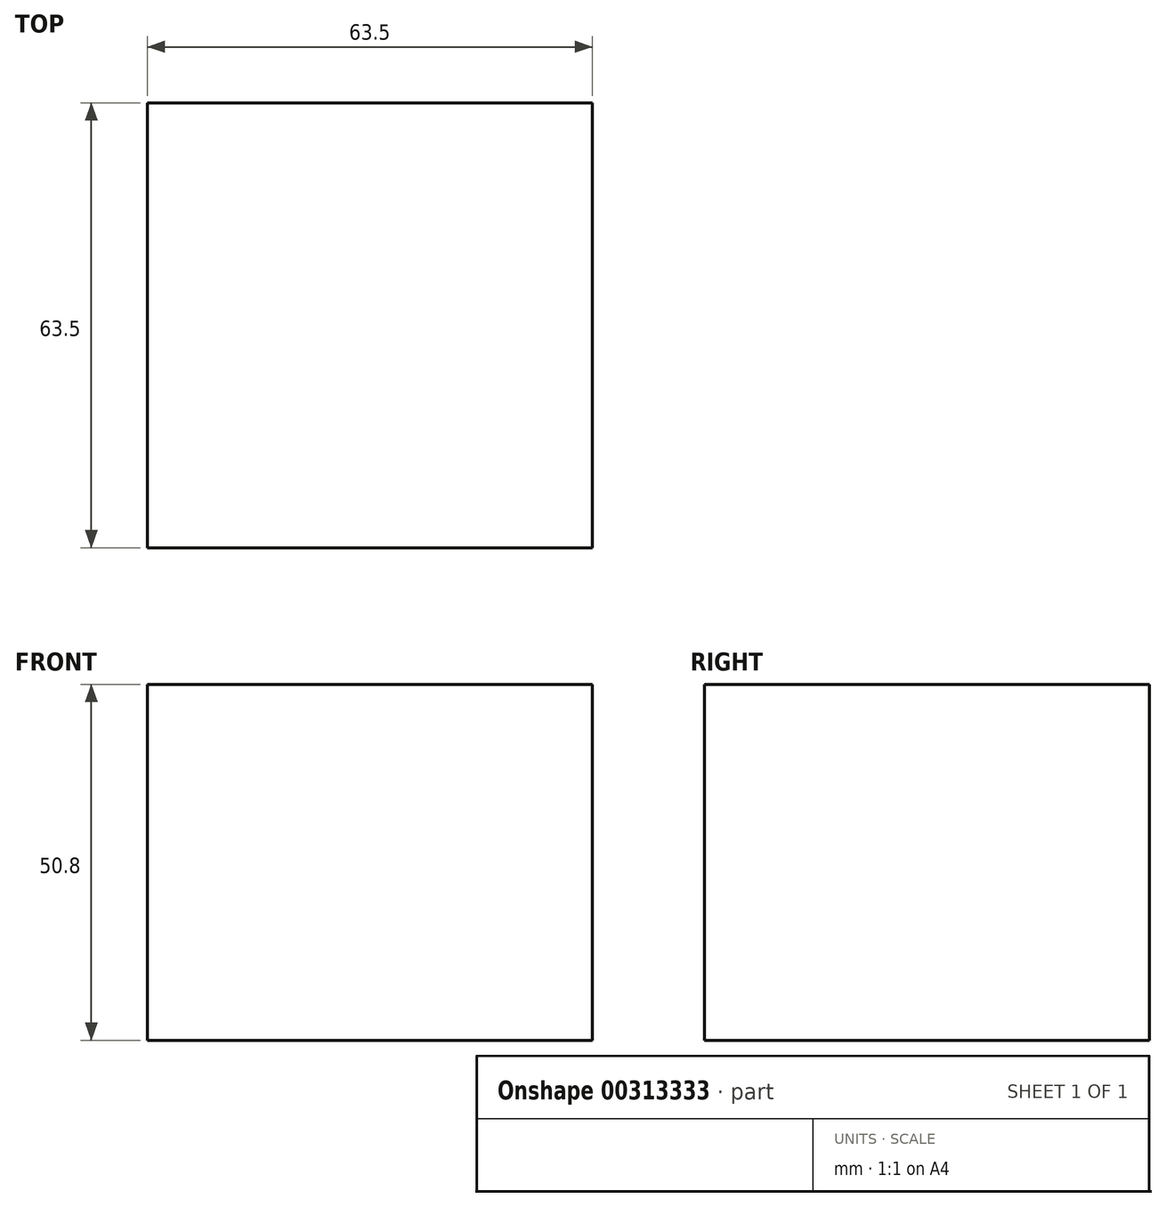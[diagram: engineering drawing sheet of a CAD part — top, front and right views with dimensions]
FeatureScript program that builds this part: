
annotation { "Feature Type Name" : "Feature", "Feature Type Description" : "" }
export const myFeature = defineFeature(function(context is Context, id is Id, definition is map)
    precondition{}
    {
        {
            var Q0;
            Q0=qCreatedBy(makeId("Front.planeOp"),FACE);
            var sketch = newSketch(context, id + "F0", { "sketchPlane" : qUnion([Q0])});
            skLineSegment(sketch, "E0", {"start": v(-32.37, -66.7) * mm, "end": v(31.13, -66.7) * mm});
            skLineSegment(sketch, "E1", {"start": v(31.13, -66.7) * mm, "end": v(31.13, -15.9) * mm});
            skLineSegment(sketch, "E2", {"start": v(31.13, -15.9) * mm, "end": v(-32.37, -15.9) * mm});
            skLineSegment(sketch, "E3", {"start": v(-32.37, -66.7) * mm, "end": v(-32.37, -15.9) * mm});
            skSolve(sketch);
        }
        {
            var Q0;
            Q0=makeQuery(id+"F0.imprint","IMPRINT",FACE,{"disambiguationData":[TD([[makeQuery(id+"F0.imprint","IMPRINT",EDGE,{"derivedFrom":sQuery(id+"F0.wireOp",EDGE,"E0")}),1.0]])]});
            extrude(context, id + "F1", {"entities" : qUnion([Q0]), "depth" : 63.5 * mm});
        }
    });
